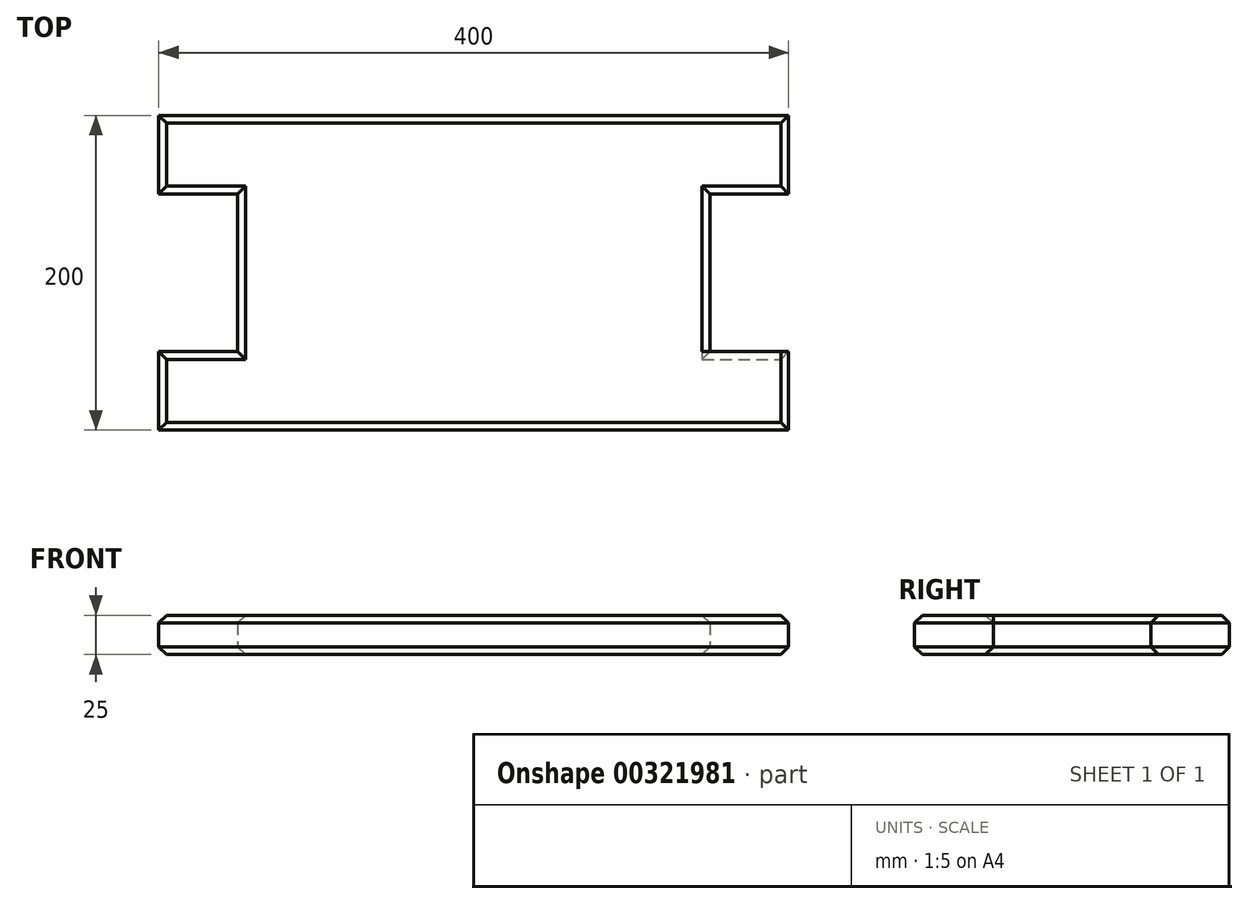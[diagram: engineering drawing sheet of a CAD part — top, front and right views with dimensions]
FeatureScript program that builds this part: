
annotation { "Feature Type Name" : "Feature", "Feature Type Description" : "" }
export const myFeature = defineFeature(function(context is Context, id is Id, definition is map)
    precondition{}
    {
        {
            var Q0;
            Q0=qCreatedBy(makeId("Top.planeOp"),FACE);
            var sketch = newSketch(context, id + "F0", { "sketchPlane" : qUnion([Q0])});
            skLineSegment(sketch, "E0.bottom", {"start": v(0, 0) * mm, "end": v(400, 0) * mm});
            skLineSegment(sketch, "E0.top", {"start": v(0, 200) * mm, "end": v(400, 200) * mm});
            skLineSegment(sketch, "E0.left", {"start": v(0, 0) * mm, "end": v(0, 200) * mm});
            skLineSegment(sketch, "E0.right", {"start": v(400, 0) * mm, "end": v(400, 200) * mm});
            skLineSegment(sketch, "E1.bottom", {"start": v(0, 150) * mm, "end": v(50, 150) * mm});
            skLineSegment(sketch, "E1.top", {"start": v(0, 50) * mm, "end": v(50, 50) * mm});
            skLineSegment(sketch, "E1.left", {"start": v(0, 150) * mm, "end": v(0, 50) * mm});
            skLineSegment(sketch, "E1.right", {"start": v(50, 150) * mm, "end": v(50, 50) * mm});
            skLineSegment(sketch, "E2", {"start": v(0, 100) * mm, "end": v(400, 100) * mm, "construction": true});
            skLineSegment(sketch, "E3", {"start": v(200, 200) * mm, "end": v(200, 0) * mm, "construction": true});
            skLineSegment(sketch, "E4.MirrorCS", {"start": v(400, 150) * mm, "end": v(350, 150) * mm});
            skLineSegment(sketch, "E5.MirrorCS", {"start": v(350, 150) * mm, "end": v(350, 50) * mm});
            skLineSegment(sketch, "E6.MirrorCS", {"start": v(400, 50) * mm, "end": v(350, 50) * mm});
            skLineSegment(sketch, "E7.MirrorCS", {"start": v(400, 150) * mm, "end": v(400, 50) * mm});
            skSolve(sketch);
        }
        {
            var Q0;
            {var subQ6=sQuery(id+"F0.wireOp",EDGE,"E0.bottom");Q0=makeQuery(id+"F0.imprint","IMPRINT",FACE,{"disambiguationData":[TD([[makeQuery(id+"F0.imprint","IMPRINT",EDGE,{"derivedFrom":subQ6}),1.0]])]});}
            extrude(context, id + "F1", {"entities" : qUnion([Q0]), "depth" : 25 * mm});
        }
        {
            var Q0;
            Q0=makeQuery(id+"F1.opExtrude","CAP_EDGE",EDGE,{"disambiguationData":[OSD([sQuery(id+"F0.wireOp",EDGE,"E0.bottom")])],"isStart":false});
            chamfer(context, id + "F2", {"entities" : qUnion([Q0]), "width" : 5 * mm, "tangentPropagation" : true});
        }
        {
            var Q0;
            Q0=makeQuery(id+"F1.opExtrude","CAP_EDGE",EDGE,{"disambiguationData":[OSD([sQuery(id+"F0.wireOp",EDGE,"E0.top")])],"isStart":false});
            chamfer(context, id + "F3", {"entities" : qUnion([Q0]), "width" : 5 * mm, "tangentPropagation" : true});
        }
        {
            var Q0;
            {var subQ0=sQuery(id+"F0.wireOp",EDGE,"E0.left");Q0=makeQuery(id+"F1.opExtrude","CAP_EDGE",EDGE,{"disambiguationData":[OSD([subQ0]),TDD([makeQuery(id+"F0.imprint","IMPRINT",EDGE,{"disambiguationData":[TD([[makeQuery(id+"F0.imprint","INTERSECT",VERTEX,{"derivedFrom":[sQuery(id+"F0.wireOp",EDGE,"E0.top"),subQ0]}),1.0]])],"derivedFrom":subQ0})])],"isStart":false});}
            var Q1;
            Q1=makeQuery(id+"F1.opExtrude","CAP_EDGE",EDGE,{"disambiguationData":[OSD([sQuery(id+"F0.wireOp",EDGE,"E1.bottom")])],"isStart":false});
            var Q2;
            Q2=makeQuery(id+"F1.opExtrude","CAP_EDGE",EDGE,{"disambiguationData":[OSD([sQuery(id+"F0.wireOp",EDGE,"E1.right")])],"isStart":false});
            var Q3;
            Q3=makeQuery(id+"F1.opExtrude","CAP_EDGE",EDGE,{"disambiguationData":[OSD([sQuery(id+"F0.wireOp",EDGE,"E1.top")])],"isStart":false});
            var Q4;
            {var subQ0=sQuery(id+"F0.wireOp",EDGE,"E0.left");Q4=makeQuery(id+"F1.opExtrude","CAP_EDGE",EDGE,{"disambiguationData":[OSD([subQ0]),TDD([makeQuery(id+"F0.imprint","IMPRINT",EDGE,{"disambiguationData":[TD([[makeQuery(id+"F0.imprint","INTERSECT",VERTEX,{"derivedFrom":[sQuery(id+"F0.wireOp",EDGE,"E0.bottom"),subQ0]}),-1.0]])],"derivedFrom":subQ0})])],"isStart":false});}
            var Q5;
            {var subQ0=sQuery(id+"F0.wireOp",EDGE,"E0.right");Q5=makeQuery(id+"F1.opExtrude","CAP_EDGE",EDGE,{"disambiguationData":[OSD([subQ0]),TDD([makeQuery(id+"F0.imprint","IMPRINT",EDGE,{"disambiguationData":[TD([[makeQuery(id+"F0.imprint","INTERSECT",VERTEX,{"derivedFrom":[sQuery(id+"F0.wireOp",EDGE,"E0.bottom"),subQ0]}),-1.0]])],"derivedFrom":subQ0})])],"isStart":false});}
            var Q6;
            Q6=makeQuery(id+"F1.opExtrude","CAP_EDGE",EDGE,{"disambiguationData":[OSD([sQuery(id+"F0.wireOp",EDGE,"E5.MirrorCS")])],"isStart":false});
            var Q7;
            Q7=makeQuery(id+"F1.opExtrude","CAP_EDGE",EDGE,{"disambiguationData":[OSD([sQuery(id+"F0.wireOp",EDGE,"E4.MirrorCS")])],"isStart":false});
            var Q8;
            {var subQ0=sQuery(id+"F0.wireOp",EDGE,"E0.right");Q8=makeQuery(id+"F1.opExtrude","CAP_EDGE",EDGE,{"disambiguationData":[OSD([subQ0]),TDD([makeQuery(id+"F0.imprint","IMPRINT",EDGE,{"disambiguationData":[TD([[makeQuery(id+"F0.imprint","INTERSECT",VERTEX,{"derivedFrom":[sQuery(id+"F0.wireOp",EDGE,"E0.top"),subQ0]}),1.0]])],"derivedFrom":subQ0})])],"isStart":false});}
            chamfer(context, id + "F4", {"entities" : qUnion([Q0, Q1, Q2, Q3, Q4, Q5, Q6, Q7, Q8]), "width" : 5 * mm, "tangentPropagation" : true});
        }
        {
            var Q0;
            Q0=makeQuery(id+"F1.opExtrude","CAP_EDGE",EDGE,{"disambiguationData":[OSD([sQuery(id+"F0.wireOp",EDGE,"E0.bottom")])],"isStart":true});
            var Q1;
            Q1=makeQuery(id+"F1.opExtrude","CAP_EDGE",EDGE,{"disambiguationData":[OSD([sQuery(id+"F0.wireOp",EDGE,"E0.top")])],"isStart":true});
            var Q2;
            Q2=makeQuery(id+"F1.opExtrude","CAP_EDGE",EDGE,{"disambiguationData":[OSD([sQuery(id+"F0.wireOp",EDGE,"E5.MirrorCS")])],"isStart":true});
            var Q3;
            Q3=makeQuery(id+"F1.opExtrude","CAP_EDGE",EDGE,{"disambiguationData":[OSD([sQuery(id+"F0.wireOp",EDGE,"E6.MirrorCS")])],"isStart":true});
            var Q4;
            {var subQ0=sQuery(id+"F0.wireOp",EDGE,"E0.right");Q4=makeQuery(id+"F1.opExtrude","CAP_EDGE",EDGE,{"disambiguationData":[OSD([subQ0]),TDD([makeQuery(id+"F0.imprint","IMPRINT",EDGE,{"disambiguationData":[TD([[makeQuery(id+"F0.imprint","INTERSECT",VERTEX,{"derivedFrom":[sQuery(id+"F0.wireOp",EDGE,"E0.bottom"),subQ0]}),-1.0]])],"derivedFrom":subQ0})])],"isStart":true});}
            var Q5;
            {var subQ0=sQuery(id+"F0.wireOp",EDGE,"E0.right");Q5=makeQuery(id+"F1.opExtrude","CAP_EDGE",EDGE,{"disambiguationData":[OSD([subQ0]),TDD([makeQuery(id+"F0.imprint","IMPRINT",EDGE,{"disambiguationData":[TD([[makeQuery(id+"F0.imprint","INTERSECT",VERTEX,{"derivedFrom":[sQuery(id+"F0.wireOp",EDGE,"E0.top"),subQ0]}),1.0]])],"derivedFrom":subQ0})])],"isStart":true});}
            var Q6;
            Q6=makeQuery(id+"F1.opExtrude","CAP_EDGE",EDGE,{"disambiguationData":[OSD([sQuery(id+"F0.wireOp",EDGE,"E4.MirrorCS")])],"isStart":true});
            var Q7;
            {var subQ0=sQuery(id+"F0.wireOp",EDGE,"E0.left");Q7=makeQuery(id+"F1.opExtrude","CAP_EDGE",EDGE,{"disambiguationData":[OSD([subQ0]),TDD([makeQuery(id+"F0.imprint","IMPRINT",EDGE,{"disambiguationData":[TD([[makeQuery(id+"F0.imprint","INTERSECT",VERTEX,{"derivedFrom":[sQuery(id+"F0.wireOp",EDGE,"E0.top"),subQ0]}),1.0]])],"derivedFrom":subQ0})])],"isStart":true});}
            var Q8;
            Q8=makeQuery(id+"F1.opExtrude","CAP_EDGE",EDGE,{"disambiguationData":[OSD([sQuery(id+"F0.wireOp",EDGE,"E1.bottom")])],"isStart":true});
            var Q9;
            Q9=makeQuery(id+"F1.opExtrude","CAP_EDGE",EDGE,{"disambiguationData":[OSD([sQuery(id+"F0.wireOp",EDGE,"E1.right")])],"isStart":true});
            var Q10;
            Q10=makeQuery(id+"F1.opExtrude","CAP_EDGE",EDGE,{"disambiguationData":[OSD([sQuery(id+"F0.wireOp",EDGE,"E1.top")])],"isStart":true});
            var Q11;
            {var subQ0=sQuery(id+"F0.wireOp",EDGE,"E0.left");Q11=makeQuery(id+"F1.opExtrude","CAP_EDGE",EDGE,{"disambiguationData":[OSD([subQ0]),TDD([makeQuery(id+"F0.imprint","IMPRINT",EDGE,{"disambiguationData":[TD([[makeQuery(id+"F0.imprint","INTERSECT",VERTEX,{"derivedFrom":[sQuery(id+"F0.wireOp",EDGE,"E0.bottom"),subQ0]}),-1.0]])],"derivedFrom":subQ0})])],"isStart":true});}
            chamfer(context, id + "F5", {"entities" : qUnion([Q0, Q1, Q2, Q3, Q4, Q5, Q6, Q7, Q8, Q9, Q10, Q11]), "width" : 5 * mm, "tangentPropagation" : true});
        }
    });
